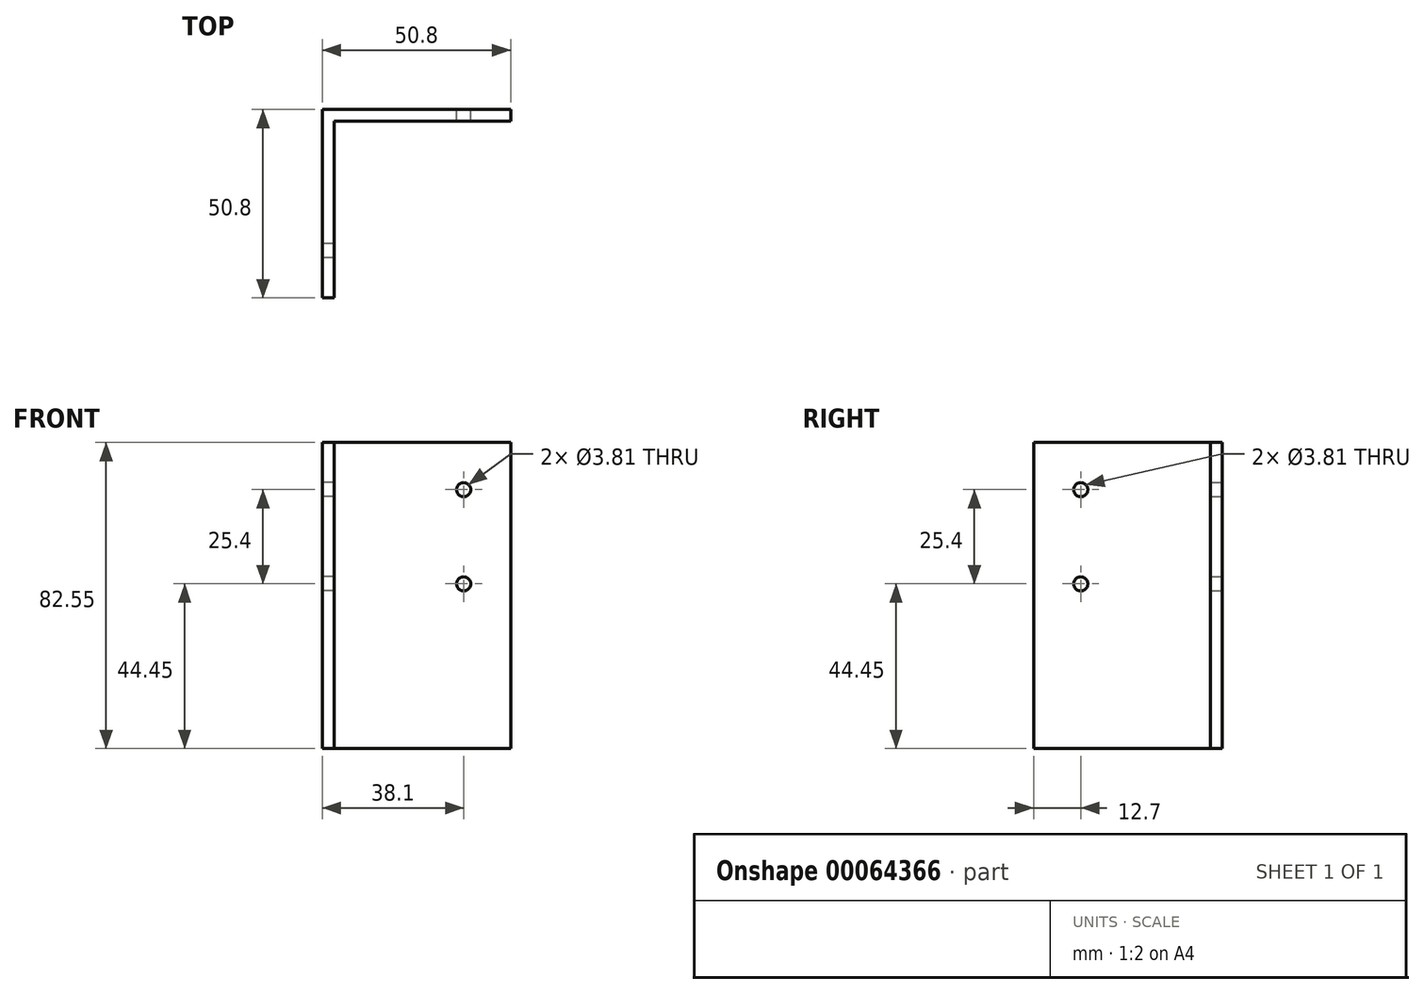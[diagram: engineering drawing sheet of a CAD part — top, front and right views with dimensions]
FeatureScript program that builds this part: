
annotation { "Feature Type Name" : "Feature", "Feature Type Description" : "" }
export const myFeature = defineFeature(function(context is Context, id is Id, definition is map)
    precondition{}
    {
        {
            var Q0;
            Q0=qCreatedBy(makeId("Top.planeOp"),FACE);
            var sketch = newSketch(context, id + "F0", { "sketchPlane" : qUnion([Q0])});
            skLineSegment(sketch, "E0.rect.bottom", {"start": v(-25.4, 25.4) * mm, "end": v(25.4, 25.4) * mm});
            skLineSegment(sketch, "E0.rect.top", {"start": v(-25.4, -25.4) * mm, "end": v(-22.23, -25.4) * mm});
            skLineSegment(sketch, "E0.rect.left", {"start": v(-25.4, 25.4) * mm, "end": v(-25.4, -25.4) * mm});
            skLineSegment(sketch, "E0.rect.right", {"start": v(25.4, 25.4) * mm, "end": v(25.4, 22.23) * mm});
            skPoint(sketch, "E0.rect.middle", {"position": v(0, 0) * mm});
            skLineSegment(sketch, "E1.rect.bottom", {"start": v(-22.23, 22.23) * mm, "end": v(25.4, 22.23) * mm});
            skLineSegment(sketch, "E1.rect.left", {"start": v(-22.22, 22.23) * mm, "end": v(-22.23, -25.4) * mm});
            skPoint(sketch, "E2.orphan", {"position": v(25.4, -25.4) * mm});
            skSolve(sketch);
        }
        {
            var Q0;
            Q0 = qSketchRegion(id + "F0", true);
            extrude(context, id + "F1", {"entities" : qUnion([Q0]), "depth" : 82.55 * mm});
        }
        {
            var Q0;
            Q0=makeQuery(id+"F1.opExtrude","SWEPT_FACE",FACE,{"disambiguationData":[OSD([sQuery(id+"F0.wireOp",EDGE,"E0.rect.left")])]});
            var sketch = newSketch(context, id + "F2", { "sketchPlane" : qUnion([Q0])});
            skPoint(sketch, "E3", {"position": v(12.7, 69.85) * mm});
            skPoint(sketch, "E4", {"position": v(12.7, 44.45) * mm});
            skSolve(sketch);
        }
        {
            var Q0;
            Q0=sQuery(id+"F2.wireOp",VERTEX,"E3");
            var Q1;
            Q1=sQuery(id+"F2.wireOp",VERTEX,"E4");
            var Q2;
            Q2=makeQuery(id+"F1.opExtrude","SWEPT_BODY",BODY,{"disambiguationData":[OSD([sQuery(id+"F0.wireOp",EDGE,"E0.rect.bottom"),sQuery(id+"F0.wireOp",EDGE,"E0.rect.top"),sQuery(id+"F0.wireOp",EDGE,"E0.rect.left"),sQuery(id+"F0.wireOp",EDGE,"E0.rect.right"),sQuery(id+"F0.wireOp",EDGE,"E1.rect.bottom"),sQuery(id+"F0.wireOp",EDGE,"E1.rect.left")])]});
            hole(context, id + "F3", {"style" : HoleStyle.SIMPLE, "holeDiameter" : 3.8 * mm, "endStyle" : HoleEndStyle.THROUGH, "locations" : qUnion([Q0, Q1]), "scope" : qUnion([Q2])});
        }
        {
            var Q0;
            Q0=makeQuery(id+"F1.opExtrude","SWEPT_FACE",FACE,{"disambiguationData":[OSD([sQuery(id+"F0.wireOp",EDGE,"E0.rect.bottom")])]});
            var sketch = newSketch(context, id + "F4", { "sketchPlane" : qUnion([Q0])});
            skPoint(sketch, "E5", {"position": v(-12.7, 69.85) * mm});
            skPoint(sketch, "E6", {"position": v(-12.7, 44.45) * mm});
            skSolve(sketch);
        }
        {
            var Q0;
            Q0=sQuery(id+"F4.wireOp",VERTEX,"E5");
            var Q1;
            Q1=sQuery(id+"F4.wireOp",VERTEX,"E6");
            var Q2;
            Q2=makeQuery(id+"F1.opExtrude","SWEPT_BODY",BODY,{"disambiguationData":[OSD([sQuery(id+"F0.wireOp",EDGE,"E0.rect.bottom"),sQuery(id+"F0.wireOp",EDGE,"E0.rect.top"),sQuery(id+"F0.wireOp",EDGE,"E0.rect.left"),sQuery(id+"F0.wireOp",EDGE,"E0.rect.right"),sQuery(id+"F0.wireOp",EDGE,"E1.rect.bottom"),sQuery(id+"F0.wireOp",EDGE,"E1.rect.left")])]});
            hole(context, id + "F5", {"style" : HoleStyle.SIMPLE, "holeDiameter" : 3.8 * mm, "endStyle" : HoleEndStyle.THROUGH, "locations" : qUnion([Q0, Q1]), "scope" : qUnion([Q2])});
        }
    });
